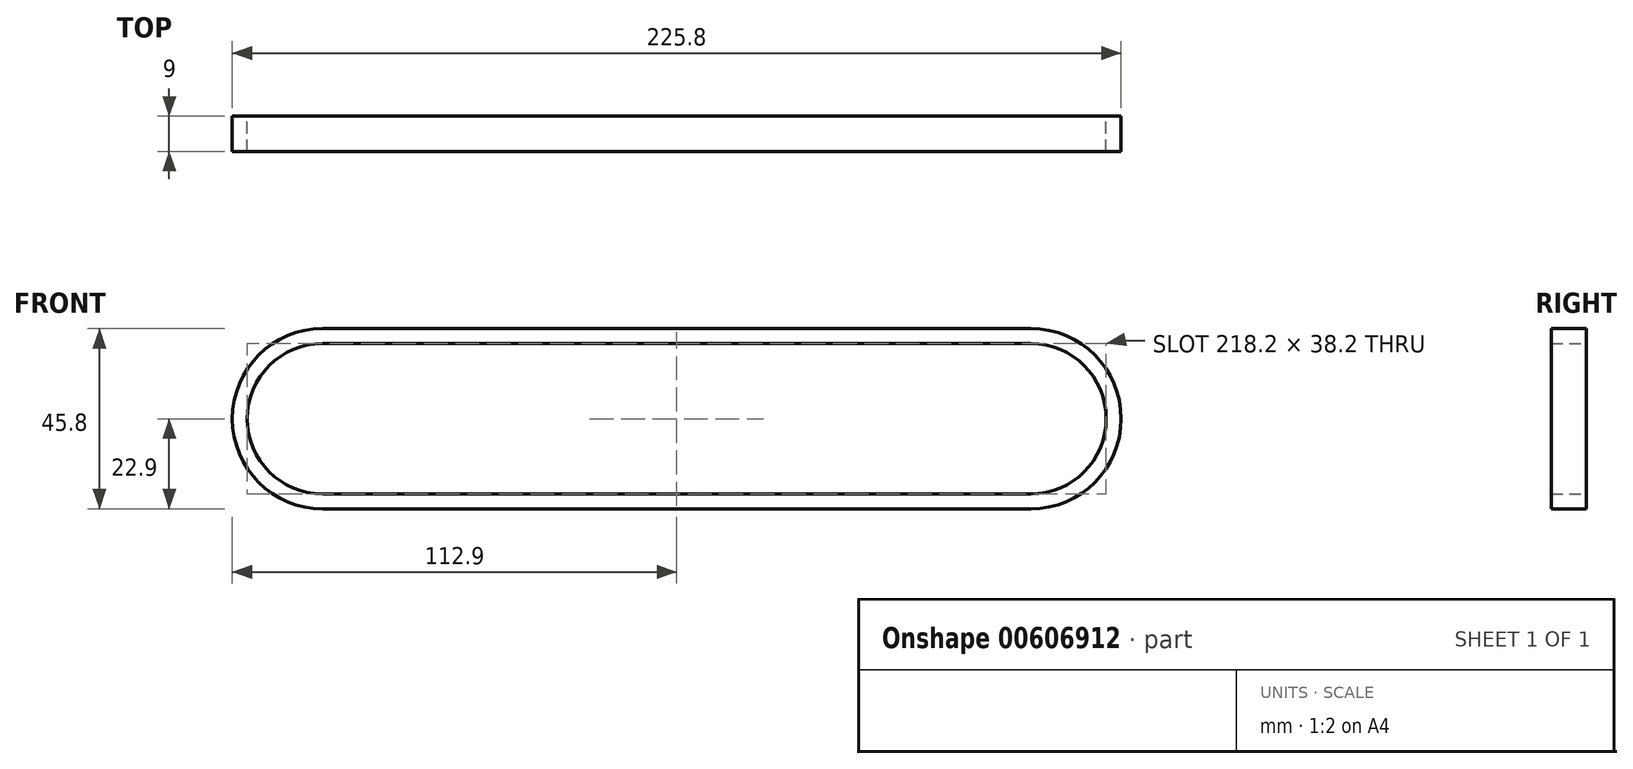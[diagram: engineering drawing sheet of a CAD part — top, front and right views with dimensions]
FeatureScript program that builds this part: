
annotation { "Feature Type Name" : "Feature", "Feature Type Description" : "" }
export const myFeature = defineFeature(function(context is Context, id is Id, definition is map)
    precondition{}
    {
        {
            var Q0;
            Q0=qCreatedBy(makeId("Front.planeOp"),FACE);
            var sketch = newSketch(context, id + "F0", { "sketchPlane" : qUnion([Q0]) });
            skArc(sketch, "E0", {"start": v(0, 21) * mm, "mid": v(-21, 0) * mm, "end": v(0, -21) * mm});
            skArc(sketch, "E1", {"start": v(180, -21) * mm, "mid": v(201, 0) * mm, "end": v(180, 21) * mm});
            skLineSegment(sketch, "E2", {"start": v(0, 21) * mm, "end": v(180, 21) * mm});
            skLineSegment(sketch, "E3", {"start": v(0, -21) * mm, "end": v(180, -21) * mm});
            skSolve(sketch);
        }
        {
            var Q0;
            Q0=qCreatedBy(makeId("Right.planeOp"),FACE);
            var sketch = newSketch(context, id + "F1", { "sketchPlane" : qUnion([Q0]) });
            skPoint(sketch, "E4.0", {"position": v(0, 21) * mm});
            skLineSegment(sketch, "E5.bottom", {"start": v(-4.5, 22.9) * mm, "end": v(4.5, 22.9) * mm});
            skLineSegment(sketch, "E5.top", {"start": v(-4.5, 19.1) * mm, "end": v(4.5, 19.1) * mm});
            skLineSegment(sketch, "E5.left", {"start": v(-4.5, 22.9) * mm, "end": v(-4.5, 19.1) * mm});
            skLineSegment(sketch, "E5.right", {"start": v(4.5, 22.9) * mm, "end": v(4.5, 19.1) * mm});
            skSolve(sketch);
        }
        {
            var Q0;
            Q0=makeQuery(id+"F1.imprint","IMPRINT",FACE,{"disambiguationData":[TD([[makeQuery(id+"F1.imprint","IMPRINT",EDGE,{"derivedFrom":sQuery(id+"F1.wireOp",EDGE,"E5.bottom")}),-1.0]])]});
            var Q1;
            Q1=sQuery(id+"F0.wireOp",EDGE,"E0");
            var Q2;
            Q2=sQuery(id+"F0.wireOp",EDGE,"E3");
            var Q3;
            Q3=sQuery(id+"F0.wireOp",EDGE,"E1");
            var Q4;
            Q4=sQuery(id+"F0.wireOp",EDGE,"E2");
            sweep(context, id + "F2", {"profiles" : qUnion([Q0]), "path" : qUnion([Q1, Q2, Q3, Q4])});
        }
    });
